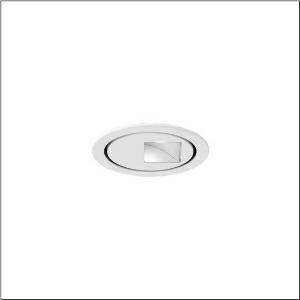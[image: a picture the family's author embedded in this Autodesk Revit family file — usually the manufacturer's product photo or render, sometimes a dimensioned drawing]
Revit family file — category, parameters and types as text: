
# Revit family: lunis_11_micro_round_51dj11b71wn21
name_source: partatom
category: Lighting Fixtures
units: mm (PartAtom-declared; Revit-internal decimal feet)

## family parameters
Cut with Voids When Loaded = No
Host = Face
Light Source = No
Part Type = Normal
Room Calculation Point = No
Round Connector Dimension = Use Diameter
Shared = No

## types (1)
- Lunis 11 micro round (1 x LED 4000K / CRI = 90 (unbekannt), 1210 lm, 4000K)
    Apparent Load = 20 VA
    CIE Flux Codes = 42 75 96 100 100
    Color Rendering = 90
    Color Temperature = 4000K
    Default Elevation = 1800 mm
    Description = Lunis 11 micro round, downlight, light control with wallwasher, of highly reflective aluminium, highly specular, light emission: direct distribution, LED rated luminous flux: 1.210lm, light colour: 940, control gear: ECG, with terminal, 3-pole, mains connection: 220..230V, AC/DC, 0/50..60Hz, LED module, luminaire module, of aluminium, highly specular, white, diameter: 114mm, clamping range: 1..40mm, recessing ring, of plastic, traffic white (RAL 9016), protection rating (complete): IP20, insulation class (complete): insulation class II (safety insulation), certification: CE, permissible ambient temperature for indoor applications: 0..+35°C, packaging unit: 1 piece
    Height = 0 mm  [stored 0 ft]
    Lamp = 1 x LED 4000K / CRI >= 90 (unbekannt)
    Lamp Light Flux = 1210 lm
    Lamp count = 1
    Length = 114 mm
    Luminous efficacy = 61 lm/W
    Manufacturer = Siteco
    ModVariant = No
    Model = 51DJ11B71WN21
    Mounting Place = Ceiling
    Mounting Type = Recessed
    Number of Poles = 1
    OnlyDefault = Yes
    Power Factor = 1
    Product Name = Lunis 11 micro round
    Product group = downlight | ceiling recessed
    ProductGroupID = 402
    Protection Class = Protection class II
    Protection Degree = IP 20
    RLX_Detail_Level = 1
    RlxData = <blob elided: 40753 chars, md5=3b6650ac>
    Socket = socket
    Standby Power = 0 W
    System Light Flux = 1210 lm
    System Power = 20 W
    Type Comments = Product without accessories
    Type Image = l_1004773.jpg
    URL = http://relux.com
    VarID = ---
    Voltage = 0 V
    Weight = 0.00 kg
    Width = 114 mm

note: [stored X ft] marks values corroborated as IEEE doubles in the binary element streams (Revit-internal decimal feet)

## geometry (parser evidence)
native form markers: Blend x4, Sweep x9
no freeform markers — native parametric forms only
